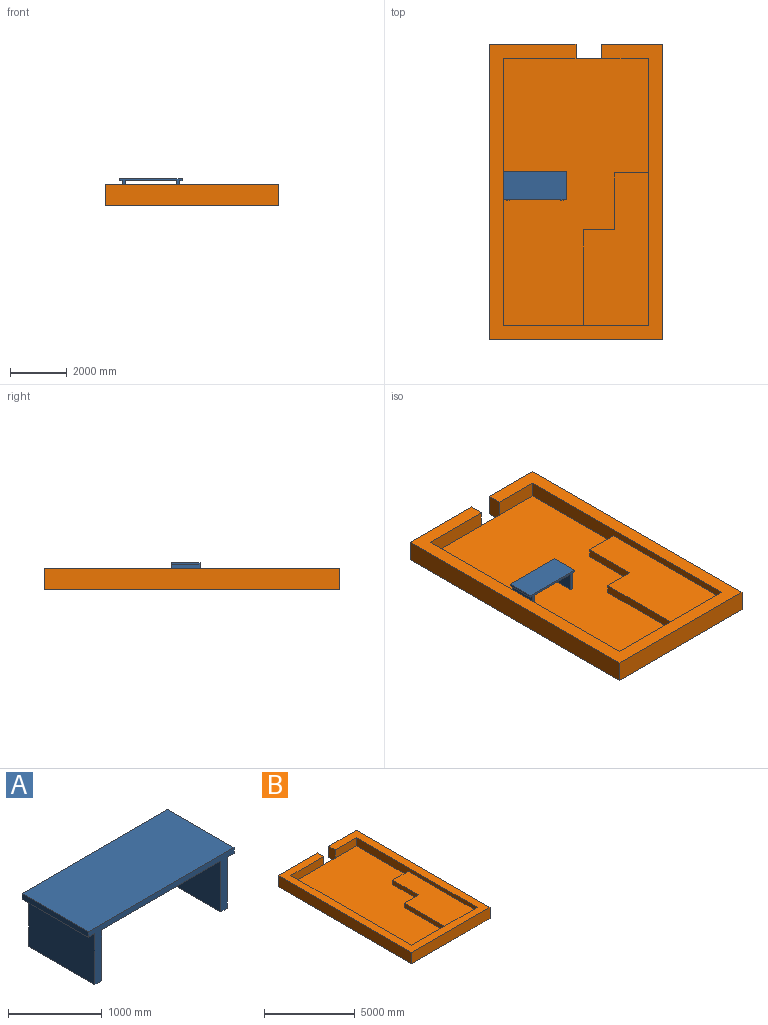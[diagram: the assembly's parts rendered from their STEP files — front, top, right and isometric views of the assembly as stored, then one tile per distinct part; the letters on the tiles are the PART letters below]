
ASSEMBLY  parts=2 mates=2
PART A: 14 faces, bbox 2200x1000x740 mm
  f0: plane 1800x1000mm, normal (0,0,-1), area 1800000mm2, adj f2,f4,f9,f11
  f1: plane 1000x100mm, normal (0,0,-1), area 100000mm2, adj f2,f4,f5,f8
  f2: plane 2200x740mm, normal (0,-1,0), area 298000mm2, adj f0,f1,f3,f5,f6,f7,f8,f9
  f3: plane 1000x75mm, normal (1,0,0), area 75000mm2, adj f2,f4,f6,f7
  f4: plane 2200x740mm, normal (0,1,0), area 298000mm2, adj f0,f1,f3,f5,f6,f7,f8,f9
  f5: plane 1000x75mm, normal (-1,0,0), area 75000mm2, adj f1,f2,f4,f6
  f6: plane 2200x1000mm, normal (0,0,1), area 2200000mm2, adj f2,f3,f4,f5
  f7: plane 1000x100mm, normal (0,0,-1), area 100000mm2, adj f2,f3,f4,f12
  f8: plane 1000x665mm, normal (-1,0,0), area 665000mm2, adj f1,f2,f4,f10
  f9: plane 1000x665mm, normal (1,0,0), area 665000mm2, adj f0,f2,f4,f10
  f10: plane 1000x100mm, normal (0,0,-1), area 100000mm2, adj f2,f4,f8,f9
  f11: plane 1000x665mm, normal (-1,0,0), area 665000mm2, adj f0,f2,f4,f13
  f12: plane 1000x665mm, normal (1,0,0), area 665000mm2, adj f2,f4,f7,f13
  f13: plane 1000x100mm, normal (0,0,-1), area 100000mm2, adj f2,f4,f11,f12
PART B: 21 faces, bbox 6100x10400x750 mm
  f0: plane 2550x550mm, normal (0,-1,0), area 1402500mm2, adj f2,f4,f17,f18
  f1: plane 3050x750mm, normal (0,1,0), area 2287500mm2, adj f2,f3,f16,f18
  f2: plane 10400x6100mm, normal (0,0,1), area 15050000mm2, adj f0,f1,f4,f5,f6,f7,f13,f14
  f3: plane 10400x6100mm, normal (0,0,-1), area 62990000mm2, adj f1,f13,f14,f15,f16,f18,f19,f20
  f4: plane 9400x550mm, normal (1,0,0), area 5170000mm2, adj f0,f2,f6,f17
  f5: plane 1650x550mm, normal (0,-1,0), area 907500mm2, adj f2,f7,f17,f20
  f6: plane 5100x550mm, normal (0,1,0), area 2115000mm2, adj f2,f4,f7,f11,f12,f17
  f7: plane 9400x550mm, normal (-1,0,0), area 3559000mm2, adj f2,f5,f6,f8,f12,f17
  f8: plane 1200x300mm, normal (0,1,0), area 360000mm2, adj f7,f9,f12,f17
  f9: plane 2000x300mm, normal (-1,0,0), area 600000mm2, adj f8,f10,f12,f17
  f10: plane 1100x300mm, normal (0,1,0), area 330000mm2, adj f9,f11,f12,f17
  f11: plane 3370x300mm, normal (-1,0,0), area 1011000mm2, adj f6,f10,f12,f17
  f12: plane 5370x2300mm, normal (0,0,1), area 10151000mm2, adj f6,f7,f8,f9,f10,f11
  f13: plane 6100x750mm, normal (0,-1,0), area 4575000mm2, adj f2,f3,f14,f16
  f14: plane 10400x750mm, normal (1,0,0), area 7800000mm2, adj f2,f3,f13,f15
  f15: plane 2150x750mm, normal (0,1,0), area 1612500mm2, adj f2,f3,f14,f20
  f16: plane 10400x750mm, normal (-1,0,0), area 7800000mm2, adj f1,f2,f3,f13
  f17: plane 9400x5100mm, normal (0,0,1), area 37789000mm2, adj f0,f4,f5,f6,f7,f8,f9,f10
  f18: plane 750x500mm, normal (1,0,0), area 375000mm2, adj f0,f1,f2,f3,f19
  f19: plane 900x200mm, normal (0,1,0), area 180000mm2, adj f3,f17,f18,f20
  f20: plane 750x500mm, normal (-1,0,0), area 375000mm2, adj f2,f3,f5,f15,f19
PLACE A t=(-4422.49,-1518.72,3778.77)mm
PLACE B t=(-2972.49,-1737.28,2913.77)mm fixed
MATE planar B.f17 <-> A.f10  axis (0,0,1) through (-3383.5,-1097.91,3113.77)mm
MATE planar B.f4 <-> A.f5  axis (1,0,0) through (-5522.49,-1737.28,3388.77)mm
